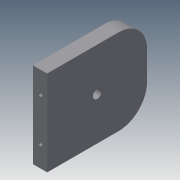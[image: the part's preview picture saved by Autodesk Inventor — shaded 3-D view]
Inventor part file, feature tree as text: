
AUTODESK INVENTOR PART (.ipt)
format: ipt  version: 2013 (Build 170138000, 138)  size: 142,336 bytes
history: native  units: mm
features: sketch x7, extrude x6, fillet x2
ambient origin geometry x8: Origin, YZ Plane, XZ Plane, XY Plane, X Axis, Y Axis, Z Axis, Center Point
bodies: Solid1 (feature_tree)
feature tree (15):
  extrude  "Extrusion1"  Depth=70.0mm
  fillet  "Fillet1"  Radius=100.0mm
  extrude  "Extrusion2"  Depth=10.0mm TaperAngle=0.0deg
  extrude  "Extrusion3"  Depth=10.0mm TaperAngle=0.0deg
  fillet  "Fillet2"  Radius=60.0mm
  extrude  "Extrusion4"  Depth=20.0mm
  extrude  "Extrusion5"  Depth=30.0mm
  extrude  "Extrusion6"  Depth=3.0mm
  sketch  "Sketch7"  dims[d17=10.0mm d18=0.0mm d19=50.0mm d20=50.0mm d21=100.0mm d22=10.0mm d23=0.0mm d24=10.0mm d25=0.0mm]
  sketch  "Sketch1"  dims[d0=50.0mm d1=70.0mm d2=100.0mm]
  sketch  "Sketch2"  dims[d3=6.0mm d4=10.0mm d5=0.0mm]
  sketch  "Sketch3"  dims[d6=50.0mm d7=10.0mm d8=0.0mm d9=60.0mm]
  sketch  "Sketch4"  dims[d10=10.0mm d11=0.0mm d12=20.0mm]
  sketch  "Sketch5"  dims[d13=15.0mm d14=30.0mm]
  sketch  "Sketch6"  dims[d15=3.0mm d16=3.0mm]
